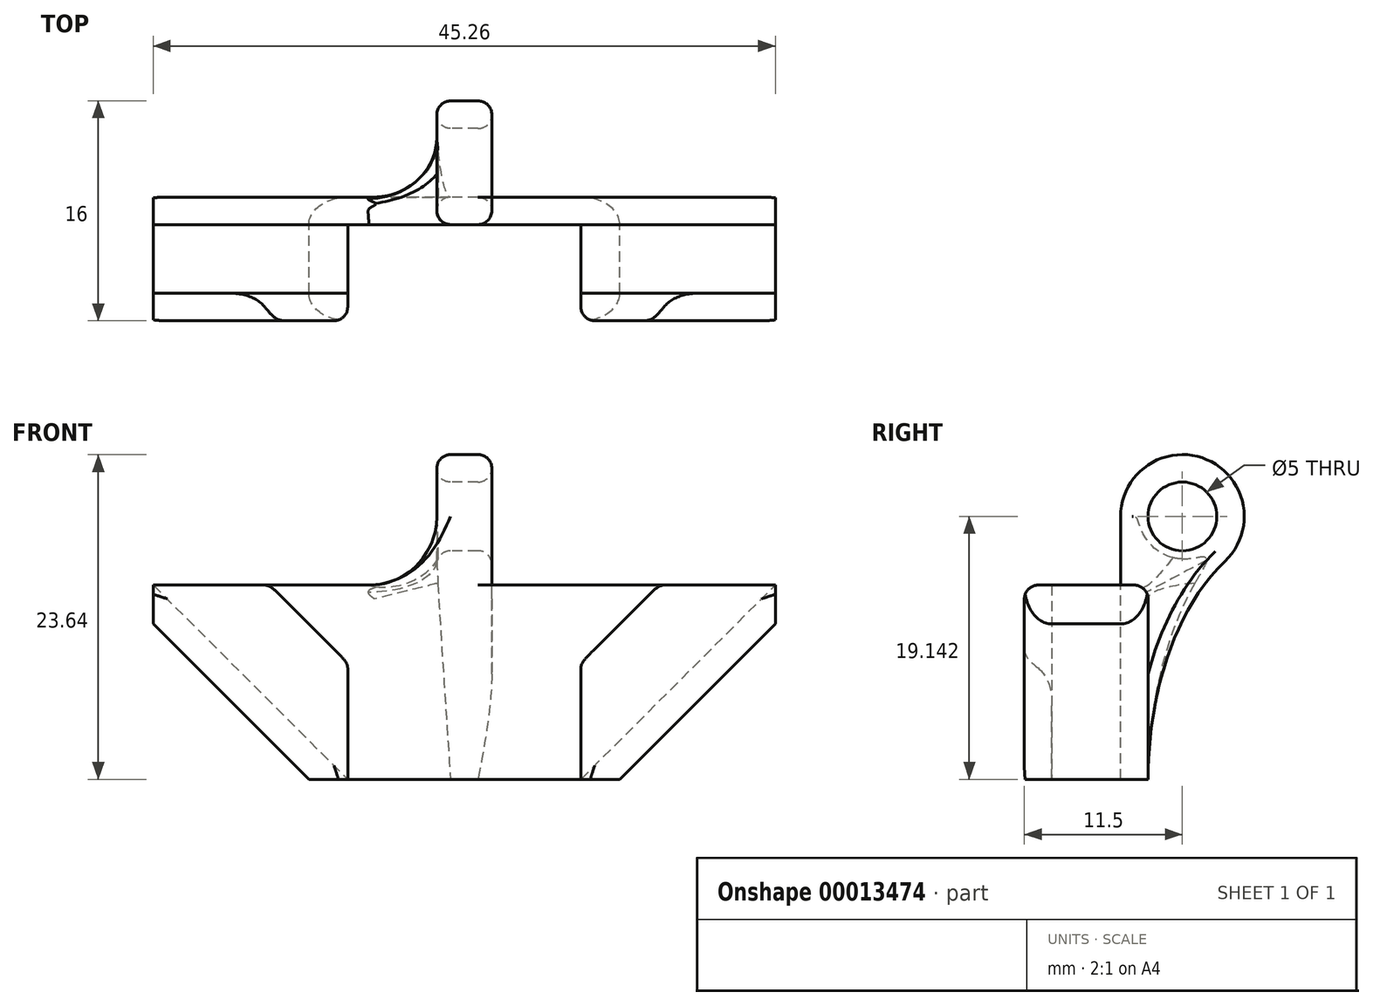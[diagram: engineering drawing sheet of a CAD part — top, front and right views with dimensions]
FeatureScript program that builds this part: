
annotation { "Feature Type Name" : "Feature", "Feature Type Description" : "" }
export const myFeature = defineFeature(function(context is Context, id is Id, definition is map)
    precondition{}
    {
        {
            var Q0;
            Q0=qCreatedBy(makeId("Front.planeOp"),FACE);
            var sketch = newSketch(context, id + "F0", { "sketchPlane" : qUnion([Q0])});
            skLineSegment(sketch, "E0", {"start": v(0, 0) * mm, "end": v(0, 14.14) * mm});
            skLineSegment(sketch, "E1", {"start": v(0, 14.14) * mm, "end": v(-25.46, 14.14) * mm});
            skLineSegment(sketch, "E2", {"start": v(0, 0) * mm, "end": v(-11.31, 0) * mm});
            skLineSegment(sketch, "E3", {"start": v(-11.31, 0) * mm, "end": v(-25.46, 14.14) * mm});
            skLineSegment(sketch, "E4", {"start": v(-11.31, 0) * mm, "end": v(-11.31, 14.14) * mm});
            skLineSegment(sketch, "E5", {"start": v(-22.63, 14.14) * mm, "end": v(-8.49, 0) * mm});
            skLineSegment(sketch, "E6", {"start": v(-14.14, 14.14) * mm, "end": v(-8.49, 8.49) * mm});
            skLineSegment(sketch, "E7", {"start": v(-8.49, 0) * mm, "end": v(-8.49, 14.14) * mm});
            skLineSegment(sketch, "E8", {"start": v(-22.63, 14.14) * mm, "end": v(-22.63, 11.31) * mm});
            skLineSegment(sketch, "E9", {"start": v(0, 0) * mm, "end": v(0, -56.69) * mm, "construction": true});
            skLineSegment(sketch, "E10", {"start": v(-8.49, 0) * mm, "end": v(0, -8.49) * mm, "construction": true});
            skLineSegment(sketch, "E11", {"start": v(-22.63, 14.14) * mm, "end": v(-24.04, 12.73) * mm, "construction": true});
            skSolve(sketch);
        }
        {
            var Q0;
            {var subQ2=sQuery(id+"F0.wireOp",EDGE,"E0");Q0=makeQuery(id+"F0.imprint","IMPRINT",FACE,{"disambiguationData":[TD([[makeQuery(id+"F0.imprint","IMPRINT",EDGE,{"derivedFrom":subQ2}),1.0]])]});}
            var Q1;
            {var subQ0=sQuery(id+"F0.wireOp",EDGE,"E7");Q1=makeQuery(id+"F0.imprint","IMPRINT",FACE,{"disambiguationData":[TD([[makeQuery(id+"F0.imprint","IMPRINT",EDGE,{"derivedFrom":subQ0}),1.0]])]});}
            var Q2;
            {var subQ0=sQuery(id+"F0.wireOp",EDGE,"E5");var subQ1=sQuery(id+"F0.wireOp",EDGE,"E4");var subQ2=makeQuery(id+"F0.imprint","INTERSECT",VERTEX,{"derivedFrom":[subQ1,subQ0]});Q2=makeQuery(id+"F0.imprint","IMPRINT",FACE,{"disambiguationData":[TD([[makeQuery(id+"F0.imprint","IMPRINT",EDGE,{"disambiguationData":[TD([[subQ2,1.0]])],"derivedFrom":subQ1}),-1.0]])]});}
            var Q3;
            {var subQ3=sQuery(id+"F0.wireOp",EDGE,"E8");Q3=makeQuery(id+"F0.imprint","IMPRINT",FACE,{"disambiguationData":[TD([[makeQuery(id+"F0.imprint","IMPRINT",EDGE,{"derivedFrom":subQ3}),1.0]])]});}
            var Q4;
            {var subQ0=sQuery(id+"F0.wireOp",EDGE,"E6");Q4=makeQuery(id+"F0.imprint","IMPRINT",FACE,{"disambiguationData":[TD([[makeQuery(id+"F0.imprint","IMPRINT",EDGE,{"derivedFrom":subQ0}),-1.0]])]});}
            var Q5;
            {var subQ0=sQuery(id+"F0.wireOp",EDGE,"E6");Q5=makeQuery(id+"F0.imprint","IMPRINT",FACE,{"disambiguationData":[TD([[makeQuery(id+"F0.imprint","IMPRINT",EDGE,{"derivedFrom":subQ0}),1.0]])]});}
            var Q6;
            {var subQ1=sQuery(id+"F0.wireOp",EDGE,"E4");var subQ3=sQuery(id+"F0.wireOp",EDGE,"E1");var subQ5=makeQuery(id+"F0.imprint","INTERSECT",VERTEX,{"derivedFrom":[subQ3,subQ1]});Q6=makeQuery(id+"F0.imprint","IMPRINT",FACE,{"disambiguationData":[TD([[makeQuery(id+"F0.imprint","IMPRINT",EDGE,{"disambiguationData":[TD([[subQ5,1.0]])],"derivedFrom":subQ1}),1.0]])]});}
            extrude(context, id + "F1", {"entities" : qUnion([Q0, Q1, Q2, Q3, Q4, Q5, Q6]), "depth" : 2 * mm});
        }
        {
            var Q0;
            {var subQ3=sQuery(id+"F0.wireOp",EDGE,"E8");Q0=makeQuery(id+"F0.imprint","IMPRINT",FACE,{"disambiguationData":[TD([[makeQuery(id+"F0.imprint","IMPRINT",EDGE,{"derivedFrom":subQ3}),1.0]])]});}
            var Q1;
            {var subQ0=sQuery(id+"F0.wireOp",EDGE,"E5");var subQ1=sQuery(id+"F0.wireOp",EDGE,"E4");var subQ2=makeQuery(id+"F0.imprint","INTERSECT",VERTEX,{"derivedFrom":[subQ1,subQ0]});Q1=makeQuery(id+"F0.imprint","IMPRINT",FACE,{"disambiguationData":[TD([[makeQuery(id+"F0.imprint","IMPRINT",EDGE,{"disambiguationData":[TD([[subQ2,1.0]])],"derivedFrom":subQ1}),-1.0]])]});}
            extrude(context, id + "F2", {"entities" : qUnion([Q0, Q1]), "operationType" : NewBodyOperationType.ADD, "depth" : 9 * mm});
        }
        {
            var Q0;
            {var subQ1=sQuery(id+"F0.wireOp",EDGE,"E4");var subQ5=sQuery(id+"F0.wireOp",EDGE,"E5");var subQ6=makeQuery(id+"F0.imprint","INTERSECT",VERTEX,{"derivedFrom":[subQ1,subQ5]});Q0=makeQuery(id+"F0.imprint","IMPRINT",FACE,{"disambiguationData":[TD([[makeQuery(id+"F0.imprint","IMPRINT",EDGE,{"disambiguationData":[TD([[subQ6,-1.0]])],"derivedFrom":subQ1}),1.0]])]});}
            var Q1;
            {var subQ3=sQuery(id+"F0.wireOp",EDGE,"E5");var subQ5=sQuery(id+"F0.wireOp",EDGE,"E4");var subQ7=makeQuery(id+"F0.imprint","INTERSECT",VERTEX,{"derivedFrom":[subQ5,subQ3]});Q1=makeQuery(id+"F0.imprint","IMPRINT",FACE,{"disambiguationData":[TD([[makeQuery(id+"F0.imprint","IMPRINT",EDGE,{"disambiguationData":[TD([[subQ7,-1.0]])],"derivedFrom":subQ5}),-1.0]])]});}
            extrude(context, id + "F3", {"entities" : qUnion([Q0, Q1]), "operationType" : NewBodyOperationType.ADD, "depth" : 9 * mm, "hasSecondDirection" : true, "secondDirectionOppositeDirection" : false, "secondDirectionDepth" : 7 * mm});
        }
        {
            var Q0;
            Q0=makeQuery(id+"F2.opExtrude","CAP_EDGE",EDGE,{"disambiguationData":[OSD([sQuery(id+"F0.wireOp",EDGE,"E3")])],"isStart":false});
            var Q1;
            Q1=makeQuery(id+"F1.opExtrude","CAP_EDGE",EDGE,{"disambiguationData":[OSD([sQuery(id+"F0.wireOp",EDGE,"E3")])],"isStart":true});
            fillet(context, id + "F4", {"entities" : qUnion([Q0, Q1]), "radius" : 2 * mm, "tangentPropagation" : true, "allowEdgeOverflow" : false});
        }
        {
            var Q0;
            Q0=makeQuery(id+"F3.opExtrude","CAP_EDGE",EDGE,{"disambiguationData":[OSD([sQuery(id+"F0.wireOp",EDGE,"E6")])],"isStart":true});
            fillet(context, id + "F5", {"entities" : qUnion([Q0]), "radius" : 2 * mm, "tangentPropagation" : true, "allowEdgeOverflow" : false});
        }
        {
            var Q0;
            {var subQ0=sQuery(id+"F0.wireOp",EDGE,"E1");var subQ1=makeQuery(id+"F1.opExtrude","CAP_EDGE",EDGE,{"disambiguationData":[OSD([subQ0])],"isStart":true});var subQ3=sQuery(id+"F0.wireOp",EDGE,"E8");Q0=makeQuery(id+"F9.boolean.opBoolean","SPLIT",EDGE,{"disambiguationData":[TD([makeQuery(id+"F1.opExtrude","SWEPT_FACE",FACE,{"disambiguationData":[OSD([subQ3])]})])],"derivedFrom":makeQuery(id+"F7.boolean.opBoolean","MERGE",EDGE,{"derivedFrom":[subQ1,makeQuery(id+"F7.opPattern","COPY",EDGE,{"derivedFrom":subQ1,"instanceName":"1"})]})});}
            var Q1;
            {var subQ0=sQuery(id+"F0.wireOp",EDGE,"E1");var subQ1=makeQuery(id+"F1.opExtrude","CAP_EDGE",EDGE,{"disambiguationData":[OSD([subQ0])],"isStart":true});var subQ2=sQuery(id+"F0.wireOp",EDGE,"E3");Q1=makeQuery(id+"F9.boolean.opBoolean","SPLIT",EDGE,{"disambiguationData":[TD([makeQuery(id+"F7.opPattern","COPY",FACE,{"derivedFrom":makeQuery(id+"F4.opFillet","BLEND_FACE",FACE,{"disambiguationData":[OSD([subQ2]),TDD([makeQuery(id+"F1.opExtrude","CAP_EDGE",EDGE,{"disambiguationData":[OSD([subQ2])],"isStart":true})])]}),"instanceName":"1"})])],"derivedFrom":makeQuery(id+"F7.boolean.opBoolean","MERGE",EDGE,{"derivedFrom":[subQ1,makeQuery(id+"F7.opPattern","COPY",EDGE,{"derivedFrom":subQ1,"instanceName":"1"})]})});}
            var Q2;
            Q2=makeQuery(id+"F3.opExtrude","CAP_EDGE",EDGE,{"disambiguationData":[OSD([sQuery(id+"F0.wireOp",EDGE,"E1")])],"isStart":false});
            var Q3;
            Q3=makeQuery(id+"F7.opPattern","COPY",EDGE,{"derivedFrom":makeQuery(id+"F3.opExtrude","CAP_EDGE",EDGE,{"disambiguationData":[OSD([sQuery(id+"F0.wireOp",EDGE,"E1")])],"isStart":false}),"instanceName":"1"});
            var Q4;
            Q4=makeQuery(id+"F3.opExtrude","CAP_EDGE",EDGE,{"disambiguationData":[OSD([sQuery(id+"F0.wireOp",EDGE,"E7")])],"isStart":false});
            var Q5;
            Q5=makeQuery(id+"F7.opPattern","COPY",EDGE,{"derivedFrom":makeQuery(id+"F3.opExtrude","CAP_EDGE",EDGE,{"disambiguationData":[OSD([sQuery(id+"F0.wireOp",EDGE,"E7")])],"isStart":false}),"instanceName":"1"});
            fillet(context, id + "F6", {"entities" : qUnion([Q0, Q1, Q2, Q3, Q4, Q5]), "radius" : 1 * mm, "tangentPropagation" : true, "allowEdgeOverflow" : false});
        }
        {
            var Q0;
            Q0=makeQuery(id+"F1.opExtrude","SWEPT_BODY",BODY,{"disambiguationData":[OSD([sQuery(id+"F0.wireOp",EDGE,"E0"),sQuery(id+"F0.wireOp",EDGE,"E1"),sQuery(id+"F0.wireOp",EDGE,"E2"),sQuery(id+"F0.wireOp",EDGE,"E3"),sQuery(id+"F0.wireOp",EDGE,"E8")])]});
            var Q1;
            Q1=qCreatedBy(makeId("Right.planeOp"),FACE);
            mirror(context, id + "F7", {"operationType" : NewBodyOperationType.ADD, "entities" : qUnion([Q0]), "mirrorPlane" : qUnion([Q1])});
        }
        {
            var Q0;
            Q0=qCreatedBy(makeId("Right.planeOp"),FACE);
            var sketch = newSketch(context, id + "F8", { "sketchPlane" : qUnion([Q0])});
            skLineSegment(sketch, "E12.0.3", {"start": v(0, 13.14) * mm, "end": v(0, 0) * mm});
            skPoint(sketch, "E13.0", {"position": v(-2, 14.14) * mm});
            skLineSegment(sketch, "E14", {"start": v(-2, 14.14) * mm, "end": v(-2, 19.14) * mm});
            skLineSegment(sketch, "E15", {"start": v(-2, 19.14) * mm, "end": v(0, 19.14) * mm, "construction": true});
            skLineSegment(sketch, "E16", {"start": v(0, 19.14) * mm, "end": v(2.5, 19.14) * mm, "construction": true});
            skCircle(sketch, "E17", {"center": v(2.5, 19.14) * mm, "radius": 2.5 * mm});
            skCircle(sketch, "E18", {"center": v(2.5, 19.14) * mm, "radius": 4.5 * mm});
            skLineSegment(sketch, "E19.0", {"start": v(-2, 14.14) * mm, "end": v(-1, 14.14) * mm});
            skArc(sketch, "E20.0.1", {"start": v(-1, 14.14) * mm, "mid": v(-0.42, 13.96) * mm, "end": v(-0.06, 13.47) * mm});
            skArc(sketch, "E20.0.2", {"start": v(-0.06, 13.47) * mm, "mid": v(-0.01, 13.31) * mm, "end": v(0, 13.14) * mm});
            skArc(sketch, "E20.0.4", {"start": v(0, 13.14) * mm, "mid": v(-0.01, 13.31) * mm, "end": v(-0.06, 13.47) * mm});
            skArc(sketch, "E20.0.5", {"start": v(-1, 14.14) * mm, "mid": v(-0.42, 13.96) * mm, "end": v(-0.06, 13.47) * mm});
            skLineSegment(sketch, "E21", {"start": v(2.5, 19.14) * mm, "end": v(0, 0) * mm, "construction": true});
            skFitSpline(sketch, "E22", {"points": [v(0, 0) * mm, v(5.6, 15.88) * mm], "startDerivative": vector(0, 16.23) * mm, "endDerivative": vector(12.08, 11.47) * mm});
            skSolve(sketch);
        }
        {
            var Q0;
            {var subQ3=sQuery(id+"F8.wireOp",EDGE,"E14");Q0=makeQuery(id+"F8.imprint","IMPRINT",FACE,{"disambiguationData":[TD([[makeQuery(id+"F8.imprint","IMPRINT",EDGE,{"derivedFrom":subQ3}),-1.0]])]});}
            var Q1;
            Q1=makeQuery(id+"F8.imprint","IMPRINT",FACE,{"disambiguationData":[TD([[makeQuery(id+"F8.imprint","IMPRINT",EDGE,{"derivedFrom":sQuery(id+"F8.wireOp",EDGE,"E17")}),-1.0]])]});
            var Q2;
            {var subQ0=sQuery(id+"F8.wireOp",EDGE,"56aa7f0c-9dca-43c1-9dc6-ce0b70c5ac08");Q2=makeQuery(id+"F8.imprint","IMPRINT",FACE,{"disambiguationData":[TD([[makeQuery(id+"F8.imprint","IMPRINT",EDGE,{"derivedFrom":subQ0}),1.0]])]});}
            extrude(context, id + "F9", {"entities" : qUnion([Q0, Q1, Q2]), "operationType" : NewBodyOperationType.ADD, "endBound" : BoundingType.SYMMETRIC, "depth" : 4 * mm});
        }
        {
            var Q0;
            Q0=makeQuery(id+"F9.opExtrude","SWEPT_FACE",FACE,{"disambiguationData":[OSD([sQuery(id+"F8.wireOp",EDGE,"E18")])]});
            var Q1;
            Q1=makeQuery(id+"F9.opExtrude","SWEPT_FACE",FACE,{"disambiguationData":[OSD([sQuery(id+"F8.wireOp",EDGE,"E17")])]});
            fillet(context, id + "F10", {"entities" : qUnion([Q0, Q1]), "radius" : 1 * mm, "tangentPropagation" : true, "allowEdgeOverflow" : false});
        }
        {
            var Q0;
            Q0=makeQuery(id+"F9.opExtrude","CAP_EDGE",EDGE,{"disambiguationData":[OSD([sQuery(id+"F8.wireOp",EDGE,"E12.0.3")])],"isStart":true});
            var Q1;
            Q1=makeQuery(id+"F9.opExtrude","CAP_EDGE",EDGE,{"disambiguationData":[OSD([sQuery(id+"F8.wireOp",EDGE,"E12.0.3")])],"isStart":false});
            fillet(context, id + "F11", {"entities" : qUnion([Q0, Q1]), "radius" : 5 * mm, "tangentPropagation" : true, "allowEdgeOverflow" : false});
        }
    });
